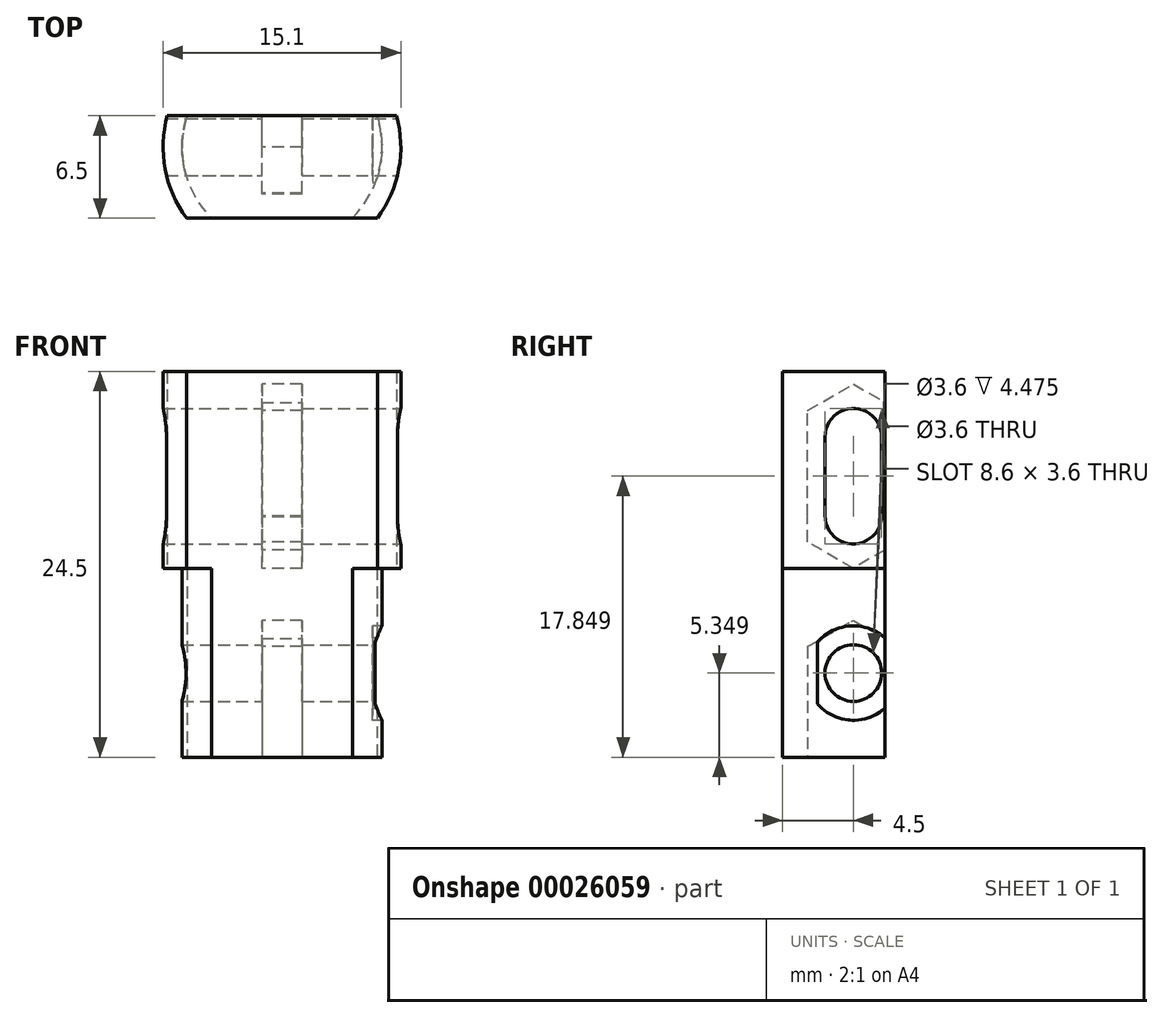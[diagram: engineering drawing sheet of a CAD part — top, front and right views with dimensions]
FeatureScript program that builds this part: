
annotation { "Feature Type Name" : "Feature", "Feature Type Description" : "" }
export const myFeature = defineFeature(function(context is Context, id is Id, definition is map)
    precondition{}
    {
        {
            var Q0;
            Q0=qCreatedBy(makeId("Top.planeOp"),FACE);
            var sketch = newSketch(context, id + "F0", { "sketchPlane" : qUnion([Q0])});
            skArc(sketch, "E0", {"start": v(-6.03, 2) * mm, "mid": v(-6.18, -1.47) * mm, "end": v(-4.48, -4.5) * mm});
            skLineSegment(sketch, "E1", {"start": v(-6.03, 2) * mm, "end": v(6.03, 2) * mm});
            skLineSegment(sketch, "E2", {"start": v(-4.48, -4.5) * mm, "end": v(4.48, -4.5) * mm});
            skArc(sketch, "E3.trimOffspring", {"start": v(4.48, -4.5) * mm, "mid": v(6.18, -1.47) * mm, "end": v(6.03, 2) * mm});
            skSolve(sketch);
        }
        {
            var Q0;
            Q0=qSketchRegion(id+"F0",true);
            extrude(context, id + "F1", {"entities" : qUnion([Q0]), "depth" : 12 * mm});
        }
        {
            var Q0;
            Q0=qCreatedBy(makeId("Right.planeOp"),FACE);
            cPlane(context, id + "F2", {"entities" : qUnion([Q0]), "cplaneType" : CPlaneType.OFFSET, "offset" : 1 * mm, "width" : 150 * mm, "height" : 150 * mm});
        }
        {
            var Q0;
            Q0=qCreatedBy(makeId("Right.planeOp"),FACE);
            var sketch = newSketch(context, id + "F3", { "sketchPlane" : qUnion([Q0])});
            skCircle(sketch, "E4.0", {"center": v(0, 5.35) * mm, "radius": 1.8 * mm});
            skCircle(sketch, "E5.cCircle", {"center": v(0, 5.35) * mm, "radius": 2.9 * mm, "construction": true});
            skLineSegment(sketch, "E5.0", {"start": v(0, 8.7) * mm, "end": v(2.9, 7.02) * mm});
            skLineSegment(sketch, "E5.1", {"start": v(2.9, 7.02) * mm, "end": v(2.9, 3.67) * mm});
            skLineSegment(sketch, "E5.2", {"start": v(2.9, 3.67) * mm, "end": v(0, 2) * mm});
            skLineSegment(sketch, "E5.3", {"start": v(0, 2) * mm, "end": v(-2.9, 3.67) * mm});
            skLineSegment(sketch, "E5.4", {"start": v(-2.9, 3.67) * mm, "end": v(-2.9, 7.02) * mm});
            skLineSegment(sketch, "E5.5", {"start": v(-2.9, 7.02) * mm, "end": v(0, 8.7) * mm});
            skPoint(sketch, "E5.0.midPoint", {"position": v(1.45, 7.86) * mm});
            skLineSegment(sketch, "E6", {"start": v(-2.9, 3.67) * mm, "end": v(-2.9, 0) * mm});
            skLineSegment(sketch, "E7", {"start": v(-2.9, 0) * mm, "end": v(2.9, 0) * mm});
            skLineSegment(sketch, "E8", {"start": v(2.9, 0) * mm, "end": v(2.9, 3.67) * mm});
            skSolve(sketch);
        }
        {
            var Q0;
            Q0=qSketchRegion(id+"F3",true);
            extrude(context, id + "F4", {"entities" : qUnion([Q0]), "operationType" : NewBodyOperationType.REMOVE, "endBound" : BoundingType.SYMMETRIC, "depth" : 2.55 * mm});
        }
        {
            var Q0;
            Q0=makeQuery(id+"F3.imprint","IMPRINT",FACE,{"disambiguationData":[TD([[makeQuery(id+"F3.imprint","IMPRINT",EDGE,{"derivedFrom":sQuery(id+"F3.wireOp",EDGE,"E4.0")}),1.0]])]});
            var Q1;
            Q1=sQuery(id+"F3.wireOp",EDGE,"E4.0");
            extrude(context, id + "F5", {"entities" : qUnion([Q0]), "operationType" : NewBodyOperationType.REMOVE, "surfaceEntities" : qUnion([Q1]), "endBound" : BoundingType.SYMMETRIC, "oppositeDirection" : true, "depth" : 25 * mm});
        }
        {
            var Q0;
            Q0=qCreatedBy(id+"F2.planeOp",FACE);
            cPlane(context, id + "F6", {"entities" : qUnion([Q0]), "cplaneType" : CPlaneType.OFFSET, "offset" : 4.75 * mm, "width" : 150 * mm, "height" : 150 * mm});
        }
        {
            var Q0;
            Q0=qCreatedBy(id+"F6.planeOp",FACE);
            var sketch = newSketch(context, id + "F7", { "sketchPlane" : qUnion([Q0])});
            skLineSegment(sketch, "E9", {"start": v(-2.28, 7.3) * mm, "end": v(-2.28, 3.4) * mm});
            skLineSegment(sketch, "E10", {"start": v(2.28, 7.3) * mm, "end": v(2.28, 3.4) * mm});
            skArc(sketch, "E11.0", {"start": v(-2.28, 7.3) * mm, "mid": v(0, 8.35) * mm, "end": v(2.28, 7.3) * mm});
            skArc(sketch, "E12", {"start": v(-2.28, 3.4) * mm, "mid": v(0, 2.35) * mm, "end": v(2.28, 3.4) * mm});
            skSolve(sketch);
        }
        {
            var Q0;
            Q0=qSketchRegion(id+"F7",true);
            extrude(context, id + "F8", {"entities" : qUnion([Q0]), "operationType" : NewBodyOperationType.REMOVE, "endBound" : BoundingType.THROUGH_ALL, "depth" : 25 * mm});
        }
        {
            var Q0;
            Q0=makeQuery(id+"F1.opExtrude","CAP_FACE",FACE,{"disambiguationData":[OSD([sQuery(id+"F0.wireOp",EDGE,"E0"),sQuery(id+"F0.wireOp",EDGE,"E1"),sQuery(id+"F0.wireOp",EDGE,"E2"),sQuery(id+"F0.wireOp",EDGE,"E3.trimOffspring")])],"isStart":false});
            var sketch = newSketch(context, id + "F9", { "sketchPlane" : qUnion([Q0])});
            skLineSegment(sketch, "E13.0", {"start": v(-6.03, 2) * mm, "end": v(0, 2) * mm});
            skLineSegment(sketch, "E14.0.3", {"start": v(0, 2) * mm, "end": v(-6.03, 2) * mm});
            skArc(sketch, "E14.0.4", {"start": v(-6.03, 2) * mm, "mid": v(-6.18, -1.47) * mm, "end": v(-4.48, -4.5) * mm});
            skLineSegment(sketch, "E14.0.5", {"start": v(-4.48, -4.5) * mm, "end": v(4.48, -4.5) * mm});
            skArc(sketch, "E14.0.6", {"start": v(4.48, -4.5) * mm, "mid": v(6.18, -1.47) * mm, "end": v(6.03, 2) * mm});
            skLineSegment(sketch, "E14.0.7", {"start": v(6.03, 2) * mm, "end": v(0, 2) * mm});
            skArc(sketch, "E15.0", {"start": v(-7.28, 2) * mm, "mid": v(-7.42, -1.4) * mm, "end": v(-6.06, -4.5) * mm});
            skArc(sketch, "E16.0", {"start": v(6.06, -4.5) * mm, "mid": v(7.42, -1.4) * mm, "end": v(7.28, 2) * mm});
            skLineSegment(sketch, "E17", {"start": v(-4.48, -4.5) * mm, "end": v(-6.06, -4.5) * mm});
            skLineSegment(sketch, "E18", {"start": v(4.48, -4.5) * mm, "end": v(6.06, -4.5) * mm});
            skLineSegment(sketch, "E19", {"start": v(-6.03, 2) * mm, "end": v(-7.28, 2) * mm});
            skLineSegment(sketch, "E20", {"start": v(6.03, 2) * mm, "end": v(7.28, 2) * mm});
            skLineSegment(sketch, "E21", {"start": v(0, 2) * mm, "end": v(0, 2) * mm});
            skSolve(sketch);
        }
        {
            var Q0;
            Q0 = qSketchRegion(id + "F9", true);
            extrude(context, id + "F10", {"entities" : qUnion([Q0]), "operationType" : NewBodyOperationType.ADD, "depth" : 12.5 * mm});
        }
        {
            var Q0;
            Q0=qCreatedBy(makeId("Right.planeOp"),FACE);
            var sketch = newSketch(context, id + "F11", { "sketchPlane" : qUnion([Q0])});
            skArc(sketch, "E22.0", {"start": v(1.8, 20.35) * mm, "mid": v(0, 22.15) * mm, "end": v(-1.8, 20.35) * mm});
            skCircle(sketch, "E23.cCircle", {"center": v(0, 20.35) * mm, "radius": 2.9 * mm, "construction": true});
            skLineSegment(sketch, "E23.0", {"start": v(0, 23.7) * mm, "end": v(2.9, 22.02) * mm});
            skLineSegment(sketch, "E23.1", {"start": v(2.9, 22.02) * mm, "end": v(2.9, 18.67) * mm});
            skLineSegment(sketch, "E23.2", {"start": v(1.45, 17.84) * mm, "end": v(-2.97, 15.29) * mm});
            skLineSegment(sketch, "E23.4", {"start": v(-2.9, 18.67) * mm, "end": v(-2.9, 22.02) * mm});
            skLineSegment(sketch, "E23.5", {"start": v(-2.9, 22.02) * mm, "end": v(0, 23.7) * mm});
            skPoint(sketch, "E23.0.midPoint", {"position": v(1.45, 22.86) * mm});
            skLineSegment(sketch, "E24", {"start": v(-2.9, 18.67) * mm, "end": v(-2.9, 18.58) * mm});
            skLineSegment(sketch, "E25", {"start": v(2.9, 18.58) * mm, "end": v(2.9, 18.67) * mm});
            skLineSegment(sketch, "E26", {"start": v(1.8, 20.35) * mm, "end": v(1.8, 15.35) * mm});
            skLineSegment(sketch, "E27", {"start": v(-1.8, 20.35) * mm, "end": v(-1.8, 15.35) * mm});
            skLineSegment(sketch, "E28.trimOffspring", {"start": v(-3.69, 16.57) * mm, "end": v(-2.68, 19.25) * mm});
            skCircle(sketch, "E29.cCircle", {"center": v(0, 15.35) * mm, "radius": 2.9 * mm, "construction": true});
            skLineSegment(sketch, "E29.0", {"start": v(2.9, 13.67) * mm, "end": v(0, 12) * mm});
            skLineSegment(sketch, "E29.1", {"start": v(0, 12) * mm, "end": v(-2.9, 13.67) * mm});
            skLineSegment(sketch, "E29.2", {"start": v(-2.9, 13.67) * mm, "end": v(-2.9, 17.02) * mm});
            skLineSegment(sketch, "E29.3", {"start": v(-1.8, 17.66) * mm, "end": v(-1.45, 17.86) * mm});
            skLineSegment(sketch, "E29.5", {"start": v(2.9, 17.02) * mm, "end": v(2.9, 13.67) * mm});
            skPoint(sketch, "E29.0.midPoint", {"position": v(1.45, 12.84) * mm});
            skLineSegment(sketch, "E30", {"start": v(2.9, 18.67) * mm, "end": v(2.9, 17.02) * mm});
            skLineSegment(sketch, "E31", {"start": v(-2.9, 18.67) * mm, "end": v(-2.9, 17.02) * mm});
            skLineSegment(sketch, "E32.trimOffspring", {"start": v(-2.97, 15.29) * mm, "end": v(-2.9, 15.25) * mm});
            skArc(sketch, "E33.trimOffspring", {"start": v(-1.8, 15.35) * mm, "mid": v(0, 13.55) * mm, "end": v(1.8, 15.35) * mm});
            skSolve(sketch);
        }
        {
            var Q0;
            Q0=makeQuery(id+"F11.imprint","IMPRINT",FACE,{"disambiguationData":[TD([[makeQuery(id+"F11.imprint","IMPRINT",EDGE,{"derivedFrom":sQuery(id+"F11.wireOp",EDGE,"E22.0")}),1.0]])]});
            extrude(context, id + "F12", {"entities" : qUnion([Q0]), "operationType" : NewBodyOperationType.REMOVE, "endBound" : BoundingType.SYMMETRIC, "oppositeDirection" : true, "depth" : 25 * mm});
        }
        {
            var Q0;
            Q0 = qSketchRegion(id + "F11", true);
            extrude(context, id + "F13", {"entities" : qUnion([Q0]), "operationType" : NewBodyOperationType.REMOVE, "endBound" : BoundingType.SYMMETRIC, "depth" : 2.55 * mm});
        }
    });
